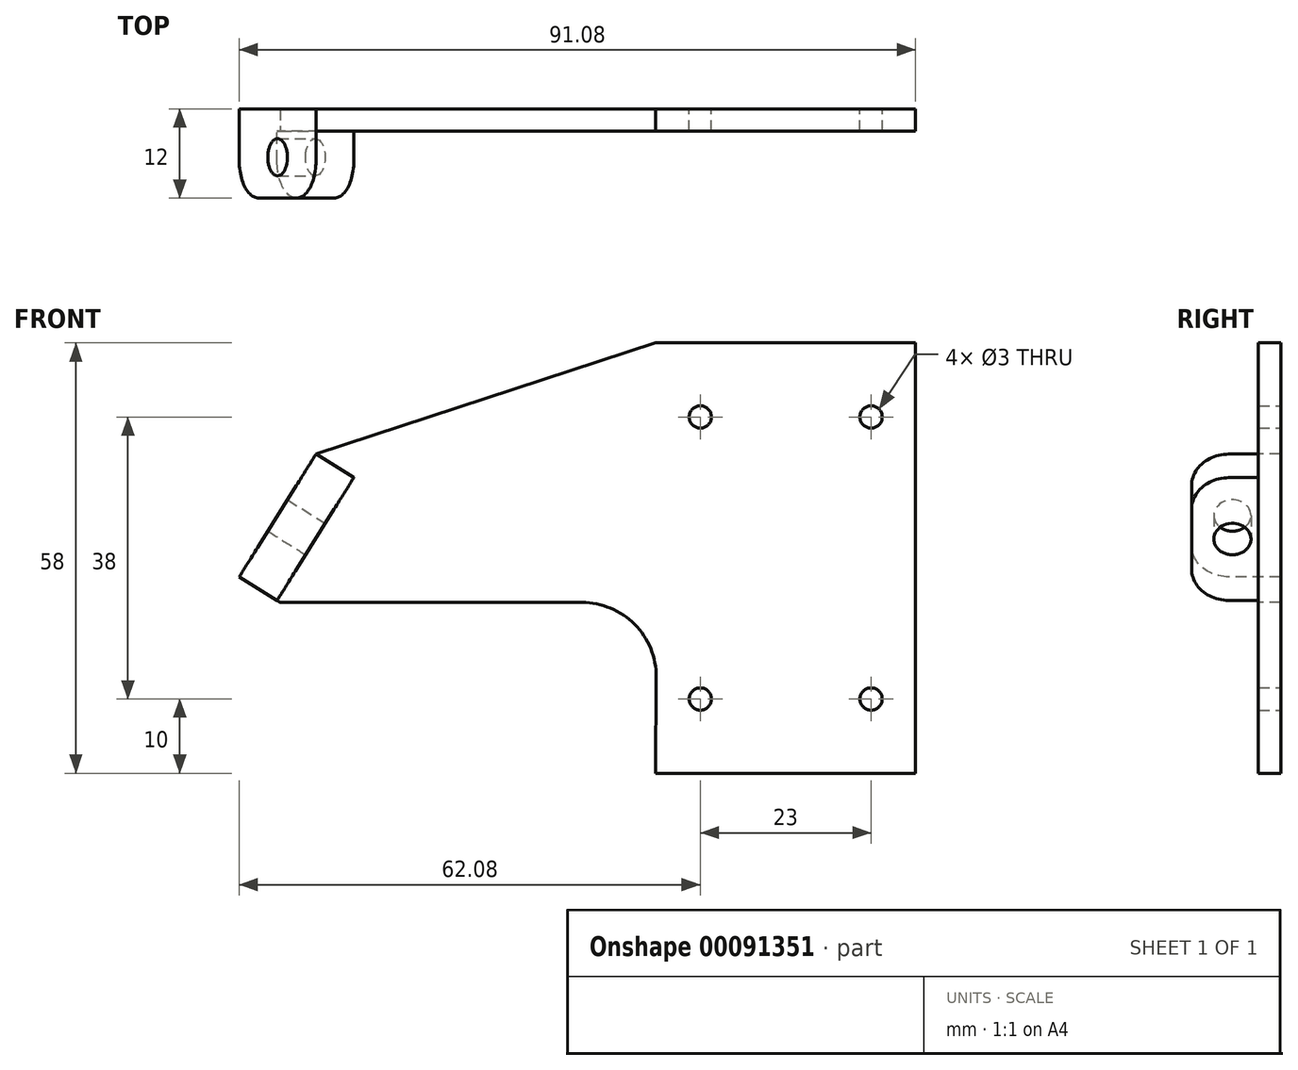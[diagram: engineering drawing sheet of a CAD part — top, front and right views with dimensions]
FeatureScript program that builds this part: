
annotation { "Feature Type Name" : "Feature", "Feature Type Description" : "" }
export const myFeature = defineFeature(function(context is Context, id is Id, definition is map)
    precondition{}
    {
        {
            var Q0;
            Q0=qCreatedBy(makeId("Front.planeOp"),FACE);
            var sketch = newSketch(context, id + "F0", { "sketchPlane" : qUnion([Q0])});
            skLineSegment(sketch, "E0", {"start": v(0, 0) * mm, "end": v(0, 58) * mm});
            skLineSegment(sketch, "E1", {"start": v(0, 58) * mm, "end": v(-35, 58) * mm});
            skLineSegment(sketch, "E2", {"start": v(-35, 58) * mm, "end": v(-80.75, 43) * mm});
            skLineSegment(sketch, "E3", {"start": v(-80.75, 43) * mm, "end": v(-91.08, 26.46) * mm});
            skLineSegment(sketch, "E4", {"start": v(-85.54, 23) * mm, "end": v(-34.88, 23) * mm});
            skLineSegment(sketch, "E5", {"start": v(-35, 0) * mm, "end": v(0, 0) * mm});
            skLineSegment(sketch, "E6", {"start": v(-87, 33) * mm, "end": v(0, 33) * mm, "construction": true});
            skLineSegment(sketch, "E7", {"start": v(-35, 58) * mm, "end": v(-35, 24.07) * mm, "construction": true});
            skLineSegment(sketch, "E8", {"start": v(-91.08, 26.46) * mm, "end": v(-85.54, 23) * mm});
            skPoint(sketch, "E9.orphan", {"position": v(-93.25, 23) * mm});
            skLineSegment(sketch, "E10", {"start": v(-35, 0) * mm, "end": v(-34.88, 23) * mm});
            skSolve(sketch);
        }
        {
            var Q0;
            Q0=makeQuery(id+"F0.imprint","IMPRINT",FACE,{"disambiguationData":[TD([[makeQuery(id+"F0.imprint","IMPRINT",EDGE,{"derivedFrom":sQuery(id+"F0.wireOp",EDGE,"E0")}),1.0]])]});
            extrude(context, id + "F1", {"entities" : qUnion([Q0]), "oppositeDirection" : true, "depth" : 3 * mm});
        }
        {
            var Q0;
            Q0=makeQuery(id+"F1.opExtrude","CAP_FACE",FACE,{"disambiguationData":[OSD([sQuery(id+"F0.wireOp",EDGE,"E0"),sQuery(id+"F0.wireOp",EDGE,"E1"),sQuery(id+"F0.wireOp",EDGE,"E2"),sQuery(id+"F0.wireOp",EDGE,"E3"),sQuery(id+"F0.wireOp",EDGE,"E4"),sQuery(id+"F0.wireOp",EDGE,"SjI2VaFg-xhUr-SC6t-RlLx-r1BLdtO8WvuT"),sQuery(id+"F0.wireOp",EDGE,"E5")])],"isStart":true});
            var sketch = newSketch(context, id + "F2", { "sketchPlane" : qUnion([Q0])});
            skLineSegment(sketch, "E11", {"start": v(-17.5, 58) * mm, "end": v(-17.5, 0) * mm, "construction": true});
            skLineSegment(sketch, "E12", {"start": v(0, 29) * mm, "end": v(-45.65, 29) * mm, "construction": true});
            skPoint(sketch, "E12.endSnap0", {"position": v(-17.5, 29) * mm});
            skPoint(sketch, "E13", {"position": v(-29, 48) * mm});
            skPoint(sketch, "E14", {"position": v(-6, 48) * mm});
            skPoint(sketch, "E15", {"position": v(-6, 10) * mm});
            skPoint(sketch, "E16", {"position": v(-29, 10) * mm});
            skSolve(sketch);
        }
        {
            var Q0;
            Q0=makeQuery(id+"F1.opExtrude","CAP_FACE",FACE,{"disambiguationData":[OSD([sQuery(id+"F0.wireOp",EDGE,"E0"),sQuery(id+"F0.wireOp",EDGE,"E1"),sQuery(id+"F0.wireOp",EDGE,"E2"),sQuery(id+"F0.wireOp",EDGE,"E3"),sQuery(id+"F0.wireOp",EDGE,"E4"),sQuery(id+"F0.wireOp",EDGE,"SjI2VaFg-xhUr-SC6t-RlLx-r1BLdtO8WvuT"),sQuery(id+"F0.wireOp",EDGE,"E5")])],"isStart":true});
            var sketch = newSketch(context, id + "F3", { "sketchPlane" : qUnion([Q0])});
            skLineSegment(sketch, "E17", {"start": v(-80.75, 43) * mm, "end": v(-91.08, 26.46) * mm});
            skLineSegment(sketch, "E18", {"start": v(-91.08, 26.46) * mm, "end": v(-86, 23.28) * mm});
            skLineSegment(sketch, "E19", {"start": v(-80.75, 43) * mm, "end": v(-75.66, 39.82) * mm});
            skLineSegment(sketch, "E20", {"start": v(-75.66, 39.82) * mm, "end": v(-86, 23.28) * mm});
            skSolve(sketch);
        }
        {
            var Q0;
            Q0=makeQuery(id+"F3.imprint","IMPRINT",FACE,{"disambiguationData":[TD([[makeQuery(id+"F3.imprint","IMPRINT",EDGE,{"derivedFrom":sQuery(id+"F3.wireOp",EDGE,"E17")}),1.0]])]});
            extrude(context, id + "F4", {"entities" : qUnion([Q0]), "operationType" : NewBodyOperationType.ADD, "depth" : 9 * mm});
        }
        {
            var Q0;
            Q0=makeQuery(id+"F4.opExtrude","CAP_EDGE",EDGE,{"disambiguationData":[OSD([sQuery(id+"F3.wireOp",EDGE,"E19")])],"isStart":false});
            var Q1;
            Q1=makeQuery(id+"F4.opExtrude","CAP_EDGE",EDGE,{"disambiguationData":[OSD([sQuery(id+"F3.wireOp",EDGE,"E18")])],"isStart":false});
            fillet(context, id + "F5", {"entities" : qUnion([Q0, Q1]), "radius" : 5 * mm, "tangentPropagation" : true, "allowEdgeOverflow" : false});
        }
        {
            var Q0;
            Q0=sQuery(id+"F2.wireOp",VERTEX,"E13");
            var Q1;
            Q1=sQuery(id+"F2.wireOp",VERTEX,"E14");
            var Q2;
            Q2=sQuery(id+"F2.wireOp",VERTEX,"E15");
            var Q3;
            Q3=sQuery(id+"F2.wireOp",VERTEX,"E16");
            var Q4;
            Q4=makeQuery(id+"F1.opExtrude","SWEPT_BODY",BODY,{"disambiguationData":[OSD([sQuery(id+"F0.wireOp",EDGE,"E0"),sQuery(id+"F0.wireOp",EDGE,"E1"),sQuery(id+"F0.wireOp",EDGE,"E2"),sQuery(id+"F0.wireOp",EDGE,"E3"),sQuery(id+"F0.wireOp",EDGE,"E4"),sQuery(id+"F0.wireOp",EDGE,"SjI2VaFg-xhUr-SC6t-RlLx-r1BLdtO8WvuT"),sQuery(id+"F0.wireOp",EDGE,"E5")])]});
            hole(context, id + "F6", {"style" : HoleStyle.SIMPLE, "endStyle" : HoleEndStyle.THROUGH, "standardTappedOrClearance" : lookupTablePath({ "standard" : "ISO", "size" : "3", "type" : "Drilled" }), "standardBlindInLast" : lookupTablePath({ "standard" : "ISO", "size" : "3", "type" : "Drilled" }), "holeDiameter" : 3 * mm, "locations" : qUnion([Q0, Q1, Q2, Q3]), "scope" : qUnion([Q4]), "isTappedThrough" : true, "startStyle" : HoleStartStyle.SKETCH});
        }
        {
            var Q0;
            Q0=makeQuery(id+"F4.boolean.opBoolean","MERGE",FACE,{"derivedFrom":[makeQuery(id+"F1.opExtrude","SWEPT_FACE",FACE,{"disambiguationData":[OSD([sQuery(id+"F0.wireOp",EDGE,"E3")])]}),makeQuery(id+"F4.opExtrude","SWEPT_FACE",FACE,{"disambiguationData":[OSD([sQuery(id+"F3.wireOp",EDGE,"E17")])]})]});
            var sketch = newSketch(context, id + "F7", { "sketchPlane" : qUnion([Q0])});
            skLineSegment(sketch, "E21", {"start": v(-3, -16.08) * mm, "end": v(9, -16.08) * mm, "construction": true});
            skPoint(sketch, "E22", {"position": v(3.5, -16.08) * mm});
            skSolve(sketch);
        }
        {
            var Q0;
            Q0=sQuery(id+"F7.wireOp",VERTEX,"E22");
            var Q1;
            Q1=makeQuery(id+"F1.opExtrude","SWEPT_BODY",BODY,{"disambiguationData":[OSD([sQuery(id+"F0.wireOp",EDGE,"E0"),sQuery(id+"F0.wireOp",EDGE,"E1"),sQuery(id+"F0.wireOp",EDGE,"E2"),sQuery(id+"F0.wireOp",EDGE,"E3"),sQuery(id+"F0.wireOp",EDGE,"E4"),sQuery(id+"F0.wireOp",EDGE,"SjI2VaFg-xhUr-SC6t-RlLx-r1BLdtO8WvuT"),sQuery(id+"F0.wireOp",EDGE,"E5")])]});
            hole(context, id + "F8", {"style" : HoleStyle.SIMPLE, "endStyle" : HoleEndStyle.THROUGH, "standardTappedOrClearance" : lookupTablePath({ "standard" : "ISO", "engagement" : "75%", "pitch" : "1 mm", "size" : "M6", "type" : "Tapped" }), "standardBlindInLast" : lookupTablePath({ "standard" : "ISO", "engagement" : "75%", "pitch" : "1 mm", "size" : "M6", "type" : "Tapped" }), "holeDiameter" : 5 * mm, "locations" : qUnion([Q0]), "scope" : qUnion([Q1]), "isTappedThrough" : true, "majorDiameter" : 6 * mm, "showTappedDepth" : true, "startStyle" : HoleStartStyle.SKETCH});
        }
        {
            var Q0;
            Q0=makeQuery(id+"F1.opExtrude","SWEPT_EDGE",EDGE,{"disambiguationData":[OSD([sQuery(id+"F0.wireOp",EDGE,"E4"),sQuery(id+"F0.wireOp",EDGE,"E10")])]});
            fillet(context, id + "F9", {"entities" : qUnion([Q0]), "radius" : 10 * mm, "tangentPropagation" : true, "allowEdgeOverflow" : false});
        }
    });
